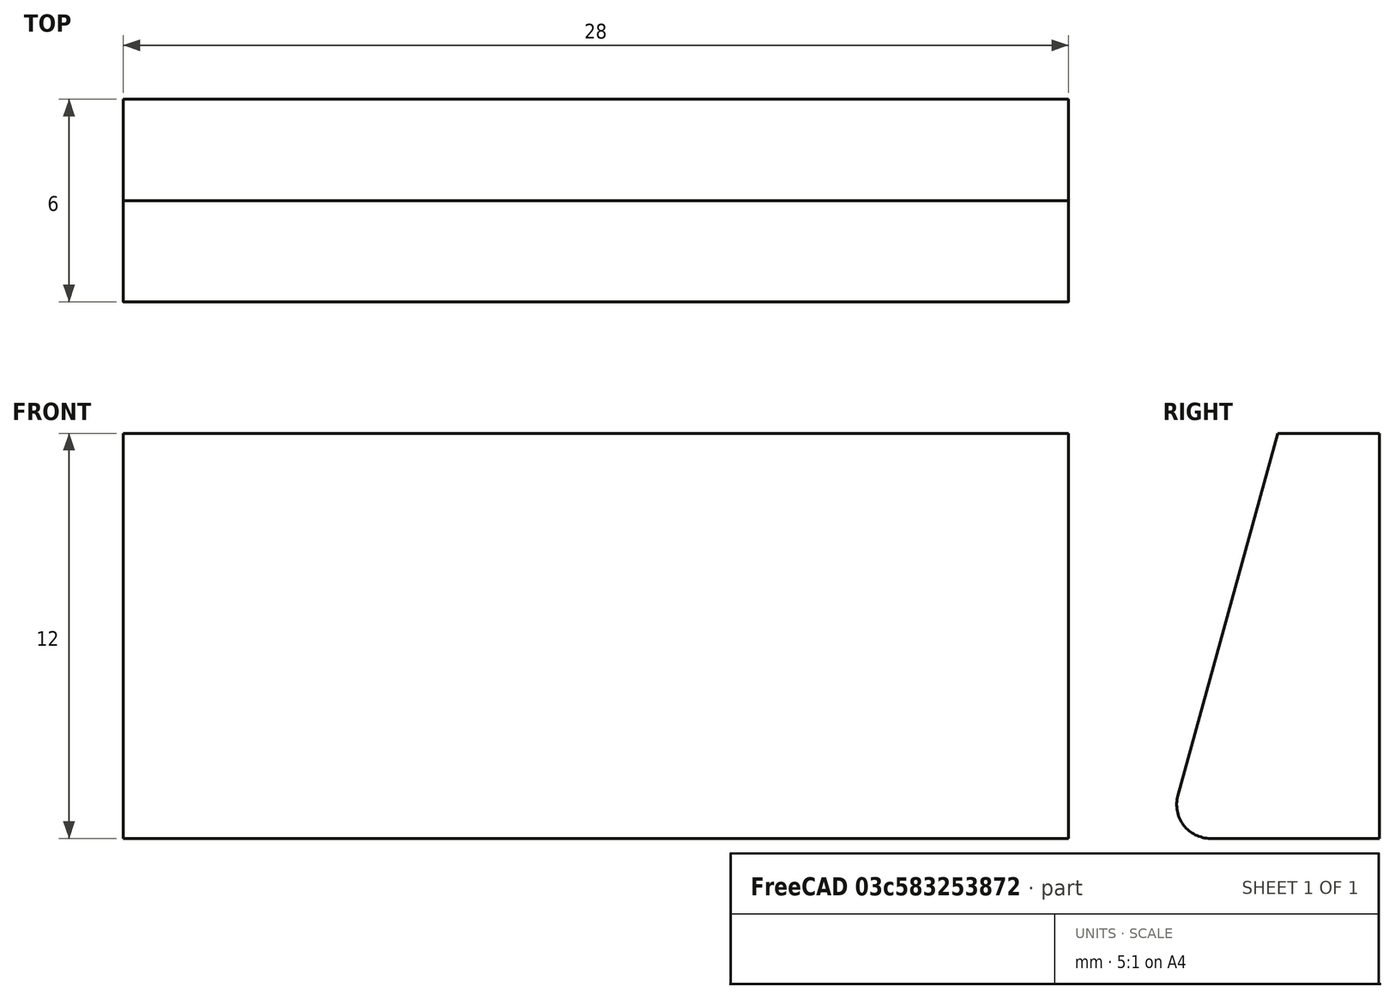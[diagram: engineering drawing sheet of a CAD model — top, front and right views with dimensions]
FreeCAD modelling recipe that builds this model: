
FCSTD DOCUMENT  (FreeCAD 0.22R37100 (Git))
Label: Opytin_buttons
License: All rights reserved
LicenseURL: http://en.wikipedia.org/wiki/All_rights_reserved
objects: Sketcher::SketchObject×1, PartDesign::Pad×1, PartDesign::Body×1
note: 4 computed .brp shape members not serialized (recipe doc carries the construction recipe); baked Part::Feature solids carry a one-line shape summary decoded from their .brp

FEATURE [Sketcher::SketchObject] Sketch
  AttachmentSupport = -> [YZ_Plane]
  FullyConstrained = true
  MapMode = 5
  Placement = pos=(0,0,0) rot=(0.57735,0.57735,0.57735;2.0944rad)
  sketch-geometry (7):
    g0: LineSegment StartX=0 StartY=0 StartZ=0 EndX=0 EndY=12 EndZ=0
    g1: LineSegment StartX=0 StartY=12 StartZ=0 EndX=-3 EndY=12 EndZ=0
    g2: LineSegment StartX=-3 StartY=12 StartZ=0 EndX=-5.96393 EndY=1.26617 EndZ=0
    g3: LineSegment StartX=-5 StartY=1.14994e-11 StartZ=0 EndX=0 EndY=0 EndZ=0
    g4: ArcOfCircle CenterX=-5 CenterY=1 CenterZ=0 NormalX=0 NormalY=0 NormalZ=1 AngleXU=0 Radius=1 StartAngle=2.87218 EndAngle=4.71239
    g5: GeomPoint X=-6.31355 Y=0 Z=0
    g6: LineSegment StartX=-6 StartY=0 StartZ=0 EndX=-6 EndY=1 EndZ=0
  constraints (18):
    c: Coincident(g-1,g0)
    c: PointOnObject(g0,g-2)
    c: Coincident(g0,g1)
    c: Horizontal(g1)
    c: Coincident(g1,g2)
    c: PointOnObject(g5,g-1)
    c: Coincident(g3,g0)
    c: PointOnObject(g5,g2)
    c: PointOnObject(g5,g3)
    c: Tangent(g2,g4) = -1.5708
    c: Tangent(g3,g4) = -1.5708
    c: DistanceX(g1,g1) = 3
    c: DistanceY(g0,g0) = 12
    c: PointOnObject(g6,g-1)
    c: Vertical(g6)
    c: Tangent(g6,g4) = 1.5708
    c: DistanceX(g6) = -6
    c: DistanceY(g6) = 1
FEATURE [PartDesign::Pad] Pad
  Direction = (1,0,0)
  Length = 28
  Length2 = 10
  Midplane = true
  Placement = pos=(0,0,0) rot=(1,1,1;2.0944rad)
  Profile = -> Sketch
  ReferenceAxis = -> Sketch [N_Axis]
  Suppressed = false
  Type = 0
FEATURE [PartDesign::Body] Body
  Group = -> [Sketch,Pad]
  Origin = -> Origin
  Tip = -> Pad
